# Revit family: Sanitary_Toilets_TOTO-USA-Inc_RPT-Wall-Hung-Toilet
name_source: partatom
category: Plumbing Fixtures
revit_build: Autodesk Revit 2015 (Build: 20140606_1530(x64)
units: mm (PartAtom-declared; Revit-internal decimal feet)

## types (1)
- CT447CFG
    BIMobject category = Toilets
    BIMobject category code = sanitary-toilets
    BIMobject main category = Sanitary
    BIMobject main category code = sanitary
    Brand url = https://www.totousa.com
    Default Elevation = 1219 mm
    Description = With a new modern D-shape, the RP wall-hung toilet saves valuable bathroom space while delivering a contempory bathroom style.
    Edition number = 1
    IFC Classification = Flow Terminal
    Installation instructions = https://www.totousa.com
    Manufacturer = TOTO
    Manufacturer name = TOTO USA Inc
    Masterformat 2014 Code = 10 28 00
    Masterformat 2014 Description = Toilet, Bath, and Laundry Accessories
    Material = Galaline - TOTO - Reinforced Marble
    Material main = Ceramics
    Model = CT447CFG
    Nominal height = 0 mm  [stored 0 ft]
    Nominal width = 0 mm  [stored 0 ft]
    OmniClass Code = 23-31 19 00
    OmniClass Description = Toilets
    Product Guid = 54bd621a-9357-4696-81b2-4ecb2ff5be0f
    Product SKU = toto-ct447cfg
    Product certification = https://www.totousa.com
    Product data url = https://bimobject.com
    Product family = Urinals
    Product group = RP???
    Product url = https://www.totousa.com
    QR code = http://bimobject.com
    Technical description = https://www.totousa.com
    Trap Seal = 54 mm
    Trap diameter = 54 mm
    UNSPSC Code = 30181505
    URL = https://www.totousa.com
    Uniclass 1.4 Code = L7216
    Uniclass 1.4 Description = Toilets
    Uniclass 2.0 Code = SS-35-65-90
    Uniclass 2.0 Description = Toilet Systems
    Uniclass 2015 Code = SL_35_80_89
    Uniclass 2015 Name = Toilets
    Uniformat II Code = D2030
    Uniformat II Description = Sanitary Waste
    Warranty = One Year Limited

note: [stored X ft] marks values corroborated as IEEE doubles in the binary element streams (Revit-internal decimal feet)

## geometry (parser evidence)
native form markers: Blend x4, Sweep x2
no freeform markers — native parametric forms only
